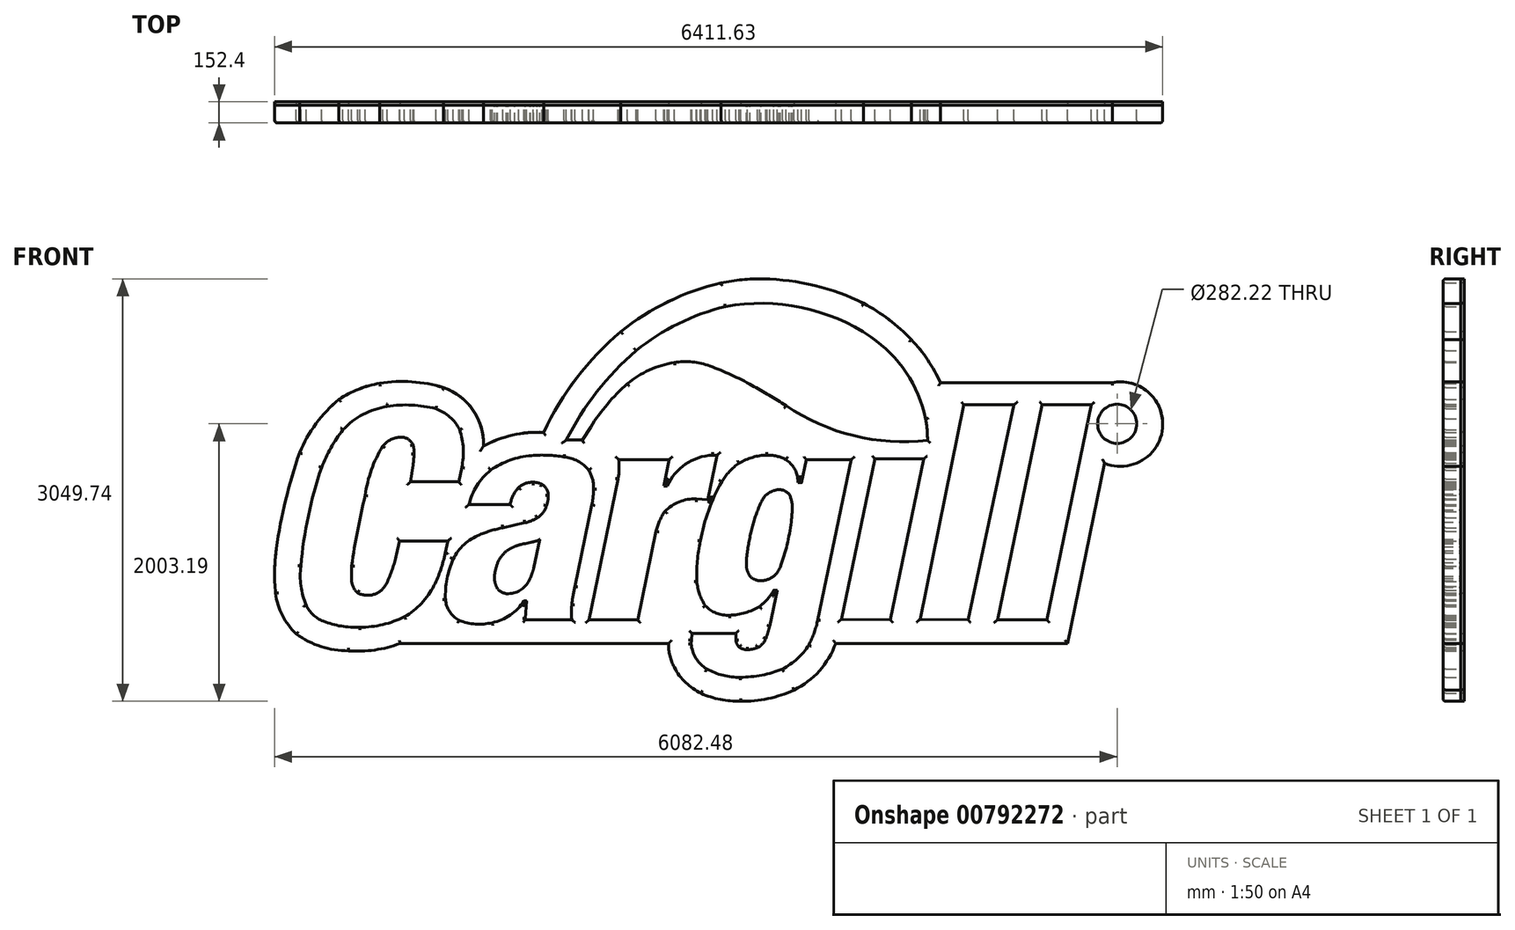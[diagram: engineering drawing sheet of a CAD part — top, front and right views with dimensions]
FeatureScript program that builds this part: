
annotation { "Feature Type Name" : "Feature", "Feature Type Description" : "" }
export const myFeature = defineFeature(function(context is Context, id is Id, definition is map)
    precondition{}
    {
        {
            var Q0;
            Q0=qCreatedBy(makeId("Front.planeOp"),FACE);
            var sketch = newSketch(context, id + "F0", { "sketchPlane" : qUnion([Q0])});
            skArc(sketch, "E0", {"start": v(-1853.74, 164.8) * mm, "mid": v(-1842.63, 301.62) * mm, "end": v(-1868.91, 436.37) * mm});
            skArc(sketch, "E1", {"start": v(-1868.91, 436.37) * mm, "mid": v(-1939.86, 529.44) * mm, "end": v(-2041.08, 588.2) * mm});
            skArc(sketch, "E2", {"start": v(-2041.08, 588.2) * mm, "mid": v(-2215, 614.67) * mm, "end": v(-2390.62, 604.46) * mm});
            skArc(sketch, "E3", {"start": v(-2390.62, 604.46) * mm, "mid": v(-2565.27, 547.67) * mm, "end": v(-2711.35, 436.37) * mm});
            skArc(sketch, "E4", {"start": v(-2711.35, 436.37) * mm, "mid": v(-2798.03, 305.5) * mm, "end": v(-2864.96, 163.5) * mm});
            skArc(sketch, "E5", {"start": v(-2864.96, 163.5) * mm, "mid": v(-2961.53, -187) * mm, "end": v(-3015.73, -546.5) * mm});
            skArc(sketch, "E6", {"start": v(-3015.73, -546.5) * mm, "mid": v(-3014.28, -691.03) * mm, "end": v(-2977.3, -830.75) * mm});
            skArc(sketch, "E7", {"start": v(-2977.3, -830.75) * mm, "mid": v(-2926.34, -899.69) * mm, "end": v(-2853.8, -945.37) * mm});
            skArc(sketch, "E8", {"start": v(-2853.8, -945.37) * mm, "mid": v(-2723.54, -981.4) * mm, "end": v(-2588.63, -989.4) * mm});
            skArc(sketch, "E9", {"start": v(-2588.63, -989.4) * mm, "mid": v(-2423.63, -970.22) * mm, "end": v(-2267.44, -913.67) * mm});
            skArc(sketch, "E10", {"start": v(-2267.44, -913.67) * mm, "mid": v(-2144.2, -816.58) * mm, "end": v(-2054.04, -688.19) * mm});
            skArc(sketch, "E11", {"start": v(-2054.04, -688.19) * mm, "mid": v(-2005.72, -573.66) * mm, "end": v(-1972.93, -453.75) * mm});
            skArc(sketch, "E12", {"start": v(-2395.81, -671.3) * mm, "mid": v(-2354.54, -570.88) * mm, "end": v(-2324.8, -466.47) * mm});
            skArc(sketch, "E13", {"start": v(-2490, -752.83) * mm, "mid": v(-2434.28, -722.02) * mm, "end": v(-2395.81, -671.3) * mm});
            skArc(sketch, "E14", {"start": v(-2605.17, -740.5) * mm, "mid": v(-2548.82, -758.18) * mm, "end": v(-2490, -752.83) * mm});
            skArc(sketch, "E15", {"start": v(-2648.28, -656.13) * mm, "mid": v(-2634.95, -702.52) * mm, "end": v(-2605.17, -740.5) * mm});
            skArc(sketch, "E16", {"start": v(-2648.28, -546.5) * mm, "mid": v(-2650.48, -601.32) * mm, "end": v(-2648.28, -656.13) * mm});
            skArc(sketch, "E17", {"start": v(-2424.98, 317.68) * mm, "mid": v(-2505.79, 147.06) * mm, "end": v(-2550.67, -36.31) * mm});
            skArc(sketch, "E18", {"start": v(-2291.59, 383.09) * mm, "mid": v(-2365.8, 365.72) * mm, "end": v(-2424.98, 317.68) * mm});
            skArc(sketch, "E19", {"start": v(-2205.97, 328.47) * mm, "mid": v(-2240.72, 368.4) * mm, "end": v(-2291.59, 383.09) * mm});
            skArc(sketch, "E20", {"start": v(-2198.16, 261.18) * mm, "mid": v(-2199.1, 295.17) * mm, "end": v(-2205.97, 328.47) * mm});
            skArc(sketch, "E21", {"start": v(-2205.6, 181.3) * mm, "mid": v(-2200.92, 221.14) * mm, "end": v(-2198.16, 261.18) * mm});
            skLineSegment(sketch, "E22", {"start": v(-2205.6, 181.3) * mm, "end": v(-2222.74, 60.72) * mm});
            skLineSegment(sketch, "E23", {"start": v(-2222.74, 60.72) * mm, "end": v(-1875.09, 60.72) * mm});
            skLineSegment(sketch, "E24", {"start": v(-1875.09, 60.72) * mm, "end": v(-1853.74, 164.8) * mm});
            skLineSegment(sketch, "E25", {"start": v(-2324.8, -466.47) * mm, "end": v(-2302.4, -366.84) * mm});
            skLineSegment(sketch, "E26", {"start": v(-2302.4, -366.84) * mm, "end": v(-1954.97, -366.84) * mm});
            skLineSegment(sketch, "E27", {"start": v(-1954.97, -366.84) * mm, "end": v(-1972.93, -453.75) * mm});
            skArc(sketch, "E28", {"start": v(-2550.67, -36.31) * mm, "mid": v(-2606.06, -290.15) * mm, "end": v(-2648.28, -546.5) * mm});
            skLineSegment(sketch, "E29", {"start": v(888.51, -931.26) * mm, "end": v(1128.72, 225.76) * mm});
            skLineSegment(sketch, "E30", {"start": v(1128.72, 225.76) * mm, "end": v(1480.56, 225.76) * mm});
            skLineSegment(sketch, "E31", {"start": v(1480.56, 225.76) * mm, "end": v(1240.36, -934.65) * mm});
            skLineSegment(sketch, "E32", {"start": v(1240.36, -934.65) * mm, "end": v(888.51, -931.26) * mm});
            skLineSegment(sketch, "E33", {"start": v(1454.71, -932.42) * mm, "end": v(1770.63, 615.9) * mm});
            skLineSegment(sketch, "E34", {"start": v(1770.63, 615.9) * mm, "end": v(2132.1, 615.9) * mm});
            skLineSegment(sketch, "E35", {"start": v(2132.1, 615.9) * mm, "end": v(1801.94, -935.26) * mm});
            skLineSegment(sketch, "E36", {"start": v(1801.94, -935.26) * mm, "end": v(1454.71, -932.42) * mm});
            skLineSegment(sketch, "E37", {"start": v(2337.02, 615.9) * mm, "end": v(2015.4, -935.26) * mm});
            skLineSegment(sketch, "E38", {"start": v(2015.4, -935.26) * mm, "end": v(2371.17, -935.26) * mm});
            skLineSegment(sketch, "E39", {"start": v(2371.17, -935.26) * mm, "end": v(2689.94, 615.9) * mm});
            skLineSegment(sketch, "E40", {"start": v(2689.94, 615.9) * mm, "end": v(2337.02, 615.9) * mm});
            skCircle(sketch, "E41", {"center": v(2877.8, 479.28) * mm, "radius": 141.1 * mm});
            skArc(sketch, "E42", {"start": v(-595.08, 1006.86) * mm, "mid": v(-879.13, 709.64) * mm, "end": v(-1098.05, 361.64) * mm});
            skArc(sketch, "E43", {"start": v(50.14, 1325.24) * mm, "mid": v(-290.23, 1202.04) * mm, "end": v(-595.08, 1006.86) * mm});
            skArc(sketch, "E44", {"start": v(1101.08, 1105.47) * mm, "mid": v(597.44, 1319.77) * mm, "end": v(50.14, 1325.24) * mm});
            skArc(sketch, "E45", {"start": v(1495.54, 516.6) * mm, "mid": v(1354.34, 848.57) * mm, "end": v(1101.08, 1105.47) * mm});
            skArc(sketch, "E46", {"start": v(1509.17, 358.66) * mm, "mid": v(1505.54, 437.9) * mm, "end": v(1495.54, 516.6) * mm});
            skArc(sketch, "E47", {"start": v(487.58, 610.95) * mm, "mid": v(975.81, 393.45) * mm, "end": v(1509.17, 358.66) * mm});
            skArc(sketch, "E48", {"start": v(-659.18, 768.54) * mm, "mid": v(-802.03, 621.55) * mm, "end": v(-923.49, 456.45) * mm});
            skArc(sketch, "E49", {"start": v(-318.77, 922.46) * mm, "mid": v(-499.03, 867.74) * mm, "end": v(-659.18, 768.54) * mm});
            skArc(sketch, "E50", {"start": v(-62.13, 896.46) * mm, "mid": v(-188.8, 925.73) * mm, "end": v(-318.77, 922.46) * mm});
            skArc(sketch, "E51", {"start": v(241.27, 757.08) * mm, "mid": v(92.44, 833.01) * mm, "end": v(-62.13, 896.46) * mm});
            skArc(sketch, "E52", {"start": v(487.58, 610.95) * mm, "mid": v(365.23, 685.38) * mm, "end": v(241.27, 757.08) * mm});
            skLineSegment(sketch, "E53", {"start": v(-923.49, 456.45) * mm, "end": v(-983.7, 361.64) * mm});
            skLineSegment(sketch, "E54", {"start": v(-983.7, 361.64) * mm, "end": v(-1098.05, 361.64) * mm});
            skArc(sketch, "E55", {"start": v(2787.2, 194.54) * mm, "mid": v(3205.58, 448.6) * mm, "end": v(2842.16, 776.5) * mm});
            skArc(sketch, "E56", {"start": v(-1645.22, 144.75) * mm, "mid": v(-1743.53, 33.23) * mm, "end": v(-1801.4, -103.72) * mm});
            skArc(sketch, "E57", {"start": v(-1351, 250.45) * mm, "mid": v(-1505.1, 217.08) * mm, "end": v(-1645.22, 144.75) * mm});
            skArc(sketch, "E58", {"start": v(-1114.36, 239.4) * mm, "mid": v(-1232.33, 252.59) * mm, "end": v(-1351, 250.45) * mm});
            skArc(sketch, "E59", {"start": v(-936.89, 144.75) * mm, "mid": v(-1016.16, 209.83) * mm, "end": v(-1114.36, 239.4) * mm});
            skArc(sketch, "E60", {"start": v(-901.92, 8.7) * mm, "mid": v(-909.62, 79.24) * mm, "end": v(-936.89, 144.75) * mm});
            skArc(sketch, "E61", {"start": v(-914.54, -105.31) * mm, "mid": v(-905.3, -48.63) * mm, "end": v(-901.92, 8.7) * mm});
            skArc(sketch, "E62", {"start": v(-1035.83, -693.63) * mm, "mid": v(-1049.72, -759.54) * mm, "end": v(-1058.93, -826.26) * mm});
            skArc(sketch, "E63", {"start": v(-1058.93, -826.26) * mm, "mid": v(-1062.94, -880.8) * mm, "end": v(-1058.93, -935.35) * mm});
            skArc(sketch, "E64", {"start": v(-1634.35, -956.35) * mm, "mid": v(-1503.9, -901.1) * mm, "end": v(-1404.74, -799.92) * mm});
            skArc(sketch, "E65", {"start": v(-1873.12, -938.04) * mm, "mid": v(-1755.2, -966.35) * mm, "end": v(-1634.35, -956.35) * mm});
            skArc(sketch, "E66", {"start": v(-1971.27, -789.36) * mm, "mid": v(-1941.6, -876.52) * mm, "end": v(-1873.12, -938.04) * mm});
            skArc(sketch, "E67", {"start": v(-1915, -497.35) * mm, "mid": v(-1960.34, -640.04) * mm, "end": v(-1971.27, -789.36) * mm});
            skArc(sketch, "E68", {"start": v(-1724.64, -321.62) * mm, "mid": v(-1835.8, -392.18) * mm, "end": v(-1915, -497.35) * mm});
            skArc(sketch, "E69", {"start": v(-1556.88, -270.9) * mm, "mid": v(-1642.04, -292.02) * mm, "end": v(-1724.64, -321.62) * mm});
            skArc(sketch, "E70", {"start": v(-1242.46, -113.42) * mm, "mid": v(-1232.17, -75.81) * mm, "end": v(-1229.71, -36.9) * mm});
            skArc(sketch, "E71", {"start": v(-1229.71, -36.9) * mm, "mid": v(-1241.56, 9.56) * mm, "end": v(-1275.57, 43.36) * mm});
            skArc(sketch, "E72", {"start": v(-1275.57, 43.36) * mm, "mid": v(-1305.97, 54.07) * mm, "end": v(-1338.06, 57.12) * mm});
            skArc(sketch, "E73", {"start": v(-1338.06, 57.12) * mm, "mid": v(-1394.55, 48.2) * mm, "end": v(-1443.54, 18.7) * mm});
            skArc(sketch, "E74", {"start": v(-1443.54, 18.7) * mm, "mid": v(-1482.62, -37.61) * mm, "end": v(-1503.74, -102.83) * mm});
            skLineSegment(sketch, "E75", {"start": v(-1801.4, -103.72) * mm, "end": v(-1503.74, -102.83) * mm});
            skArc(sketch, "E76", {"start": v(-1308.09, -199.85) * mm, "mid": v(-1267.42, -162.6) * mm, "end": v(-1242.46, -113.42) * mm});
            skArc(sketch, "E77", {"start": v(-1398.04, -235.27) * mm, "mid": v(-1351.72, -220.98) * mm, "end": v(-1308.09, -199.85) * mm});
            skLineSegment(sketch, "E78", {"start": v(-1556.88, -270.9) * mm, "end": v(-1398.04, -235.27) * mm});
            skLineSegment(sketch, "E79", {"start": v(-1035.83, -693.63) * mm, "end": v(-914.54, -105.31) * mm});
            skLineSegment(sketch, "E80", {"start": v(-1058.93, -935.35) * mm, "end": v(-1393.05, -935.35) * mm});
            skLineSegment(sketch, "E81", {"start": v(-1393.05, -935.35) * mm, "end": v(-1393.66, -925.25) * mm});
            skLineSegment(sketch, "E82", {"start": v(-1393.66, -925.25) * mm, "end": v(-1385.77, -799.35) * mm});
            skLineSegment(sketch, "E83", {"start": v(-1385.77, -799.35) * mm, "end": v(-1404.74, -799.92) * mm});
            skArc(sketch, "E84", {"start": v(-1517.46, -747.03) * mm, "mid": v(-1422.59, -716.33) * mm, "end": v(-1360.21, -638.53) * mm});
            skArc(sketch, "E85", {"start": v(-1360.21, -638.53) * mm, "mid": v(-1345.94, -601.96) * mm, "end": v(-1334.75, -564.32) * mm});
            skArc(sketch, "E86", {"start": v(-1600.82, -701.27) * mm, "mid": v(-1565.62, -735.95) * mm, "end": v(-1517.46, -747.03) * mm});
            skArc(sketch, "E87", {"start": v(-1617.05, -621.91) * mm, "mid": v(-1614.45, -662.72) * mm, "end": v(-1600.82, -701.27) * mm});
            skArc(sketch, "E88", {"start": v(-1593.8, -522.98) * mm, "mid": v(-1608.96, -571.62) * mm, "end": v(-1617.05, -621.91) * mm});
            skArc(sketch, "E89", {"start": v(-1529.83, -438.31) * mm, "mid": v(-1566.7, -476.96) * mm, "end": v(-1593.8, -522.98) * mm});
            skArc(sketch, "E90", {"start": v(-1472.28, -406.96) * mm, "mid": v(-1501.86, -421.16) * mm, "end": v(-1529.83, -438.31) * mm});
            skArc(sketch, "E91", {"start": v(-1395.4, -384.73) * mm, "mid": v(-1434.41, -393.86) * mm, "end": v(-1472.28, -406.96) * mm});
            skArc(sketch, "E92", {"start": v(-1356.2, -376.5) * mm, "mid": v(-1333.26, -371.34) * mm, "end": v(-1310.69, -364.8) * mm});
            skArc(sketch, "E93", {"start": v(-1310.69, -364.8) * mm, "mid": v(-1300.48, -359.9) * mm, "end": v(-1291.06, -353.65) * mm});
            skLineSegment(sketch, "E94", {"start": v(-1291.06, -353.65) * mm, "end": v(-1289.84, -353.65) * mm});
            skLineSegment(sketch, "E95", {"start": v(-1289.84, -353.65) * mm, "end": v(-1334.75, -564.32) * mm});
            skLineSegment(sketch, "E96", {"start": v(-1395.4, -384.73) * mm, "end": v(-1356.2, -376.5) * mm});
            skArc(sketch, "E97", {"start": v(-387.94, -153.2) * mm, "mid": v(-425.7, -221.92) * mm, "end": v(-450.55, -296.3) * mm});
            skArc(sketch, "E98", {"start": v(-160.28, -62.94) * mm, "mid": v(-283.64, -84.04) * mm, "end": v(-387.94, -153.2) * mm});
            skArc(sketch, "E99", {"start": v(-42.88, 253.05) * mm, "mid": v(-237.67, 187.9) * mm, "end": v(-370.17, 30.95) * mm});
            skArc(sketch, "E100", {"start": v(-724.98, 80.6) * mm, "mid": v(-717.66, 151.06) * mm, "end": v(-720.65, 221.83) * mm});
            skLineSegment(sketch, "E101", {"start": v(-720.65, 221.83) * mm, "end": v(-356.51, 221.83) * mm});
            skLineSegment(sketch, "E102", {"start": v(-356.51, 221.83) * mm, "end": v(-395.89, 30.95) * mm});
            skLineSegment(sketch, "E103", {"start": v(-395.89, 30.95) * mm, "end": v(-370.17, 30.95) * mm});
            skLineSegment(sketch, "E104", {"start": v(-160.28, -62.94) * mm, "end": v(-77.7, -69.74) * mm});
            skLineSegment(sketch, "E105", {"start": v(-77.7, -69.74) * mm, "end": v(-10.97, 253.27) * mm});
            skLineSegment(sketch, "E106", {"start": v(-10.97, 253.27) * mm, "end": v(-42.88, 253.05) * mm});
            skLineSegment(sketch, "E107", {"start": v(-724.98, 80.6) * mm, "end": v(-933.72, -935.84) * mm});
            skLineSegment(sketch, "E108", {"start": v(-933.72, -935.84) * mm, "end": v(-582.85, -935.84) * mm});
            skLineSegment(sketch, "E109", {"start": v(-582.85, -935.84) * mm, "end": v(-450.55, -296.3) * mm});
            skArc(sketch, "E110", {"start": v(-197.36, -1108.56) * mm, "mid": v(-162.64, -1213.34) * mm, "end": v(-84.09, -1290.87) * mm});
            skArc(sketch, "E111", {"start": v(-84.09, -1290.87) * mm, "mid": v(32.73, -1336.3) * mm, "end": v(157.28, -1350.3) * mm});
            skArc(sketch, "E112", {"start": v(157.28, -1350.3) * mm, "mid": v(312.42, -1335.05) * mm, "end": v(461.93, -1290.87) * mm});
            skArc(sketch, "E113", {"start": v(461.93, -1290.87) * mm, "mid": v(568.6, -1216.6) * mm, "end": v(652.22, -1117.08) * mm});
            skArc(sketch, "E114", {"start": v(652.22, -1117.08) * mm, "mid": v(690.73, -1028.55) * mm, "end": v(716.96, -935.64) * mm});
            skArc(sketch, "E115", {"start": v(572.85, 76.64) * mm, "mid": v(546.3, 158.5) * mm, "end": v(486.42, 220.31) * mm});
            skArc(sketch, "E116", {"start": v(486.42, 220.31) * mm, "mid": v(420.25, 246) * mm, "end": v(349.65, 253.33) * mm});
            skArc(sketch, "E117", {"start": v(349.65, 253.33) * mm, "mid": v(245.43, 237.66) * mm, "end": v(148.88, 195.38) * mm});
            skArc(sketch, "E118", {"start": v(148.88, 195.38) * mm, "mid": v(78.8, 134.98) * mm, "end": v(23.09, 61.1) * mm});
            skArc(sketch, "E119", {"start": v(23.09, 61.1) * mm, "mid": v(-71.74, -146.6) * mm, "end": v(-131.48, -366.99) * mm});
            skArc(sketch, "E120", {"start": v(-131.48, -366.99) * mm, "mid": v(-152.88, -512.22) * mm, "end": v(-156.62, -658.97) * mm});
            skArc(sketch, "E121", {"start": v(-156.62, -658.97) * mm, "mid": v(-137.02, -749.7) * mm, "end": v(-95.54, -832.74) * mm});
            skArc(sketch, "E122", {"start": v(-95.54, -832.74) * mm, "mid": v(-16.22, -887.84) * mm, "end": v(79.28, -902.25) * mm});
            skArc(sketch, "E123", {"start": v(79.28, -902.25) * mm, "mid": v(192.1, -884.73) * mm, "end": v(297, -839.73) * mm});
            skArc(sketch, "E124", {"start": v(297, -839.73) * mm, "mid": v(349.1, -791.48) * mm, "end": v(391.28, -734.35) * mm});
            skArc(sketch, "E125", {"start": v(125.8, -1081.2) * mm, "mid": v(132.95, -1110.4) * mm, "end": v(151.27, -1134.24) * mm});
            skArc(sketch, "E126", {"start": v(151.27, -1134.24) * mm, "mid": v(178.83, -1147.69) * mm, "end": v(209.3, -1151.25) * mm});
            skArc(sketch, "E127", {"start": v(209.3, -1151.25) * mm, "mid": v(245.77, -1147.43) * mm, "end": v(280.95, -1137.05) * mm});
            skArc(sketch, "E128", {"start": v(280.95, -1137.05) * mm, "mid": v(317.27, -1109.33) * mm, "end": v(341.79, -1070.79) * mm});
            skArc(sketch, "E129", {"start": v(341.79, -1070.79) * mm, "mid": v(357.27, -1026.34) * mm, "end": v(369.87, -980.98) * mm});
            skArc(sketch, "E130", {"start": v(228.15, -621.33) * mm, "mid": v(263.51, -645.84) * mm, "end": v(305.86, -653.44) * mm});
            skArc(sketch, "E131", {"start": v(305.86, -653.44) * mm, "mid": v(354.88, -644.95) * mm, "end": v(398.92, -621.8) * mm});
            skArc(sketch, "E132", {"start": v(398.92, -621.8) * mm, "mid": v(426.46, -590.15) * mm, "end": v(446.1, -553.08) * mm});
            skArc(sketch, "E133", {"start": v(446.1, -553.08) * mm, "mid": v(495, -394.18) * mm, "end": v(524.3, -230.53) * mm});
            skArc(sketch, "E134", {"start": v(202.74, -560.17) * mm, "mid": v(211.76, -592.28) * mm, "end": v(228.15, -621.33) * mm});
            skArc(sketch, "E135", {"start": v(207.4, -451.93) * mm, "mid": v(202.15, -505.92) * mm, "end": v(202.74, -560.17) * mm});
            skArc(sketch, "E136", {"start": v(246.22, -257.29) * mm, "mid": v(224, -354.05) * mm, "end": v(207.4, -451.93) * mm});
            skArc(sketch, "E137", {"start": v(311.71, -78.12) * mm, "mid": v(274.52, -166.08) * mm, "end": v(246.22, -257.29) * mm});
            skArc(sketch, "E138", {"start": v(434.98, 3.76) * mm, "mid": v(362.16, -20.34) * mm, "end": v(311.71, -78.12) * mm});
            skArc(sketch, "E139", {"start": v(508.94, -27.5) * mm, "mid": v(475.45, -3.61) * mm, "end": v(434.98, 3.76) * mm});
            skArc(sketch, "E140", {"start": v(532.27, -140.63) * mm, "mid": v(528.63, -82.4) * mm, "end": v(508.94, -27.5) * mm});
            skArc(sketch, "E141", {"start": v(524.3, -230.53) * mm, "mid": v(529.17, -185.66) * mm, "end": v(532.27, -140.63) * mm});
            skLineSegment(sketch, "E142", {"start": v(572.85, 76.64) * mm, "end": v(574.8, 53.82) * mm});
            skLineSegment(sketch, "E143", {"start": v(574.8, 53.82) * mm, "end": v(599.34, 53.82) * mm});
            skLineSegment(sketch, "E144", {"start": v(599.34, 53.82) * mm, "end": v(633.67, 221.52) * mm});
            skLineSegment(sketch, "E145", {"start": v(633.67, 221.52) * mm, "end": v(957.92, 221.52) * mm});
            skLineSegment(sketch, "E146", {"start": v(957.92, 221.52) * mm, "end": v(716.96, -935.64) * mm});
            skLineSegment(sketch, "E147", {"start": v(391.28, -734.35) * mm, "end": v(398.54, -722.3) * mm});
            skLineSegment(sketch, "E148", {"start": v(398.54, -722.3) * mm, "end": v(423.93, -722.3) * mm});
            skLineSegment(sketch, "E149", {"start": v(423.93, -722.3) * mm, "end": v(369.87, -980.98) * mm});
            skLineSegment(sketch, "E150", {"start": v(-197.36, -1108.56) * mm, "end": v(-196.23, -1081.82) * mm});
            skLineSegment(sketch, "E151", {"start": v(-196.23, -1081.82) * mm, "end": v(-192.26, -1034.4) * mm});
            skLineSegment(sketch, "E152", {"start": v(-192.26, -1034.4) * mm, "end": v(124.38, -1034.4) * mm});
            skLineSegment(sketch, "E153", {"start": v(124.38, -1034.4) * mm, "end": v(125.8, -1081.2) * mm});
            skArc(sketch, "E154", {"start": v(-1263.1, 417.63) * mm, "mid": v(-1486.7, 397.65) * mm, "end": v(-1696.84, 318.74) * mm});
            skArc(sketch, "E155", {"start": v(-705.45, 1144.69) * mm, "mid": v(-1022.9, 810.79) * mm, "end": v(-1263.1, 417.63) * mm});
            skArc(sketch, "E156", {"start": v(19.35, 1496.35) * mm, "mid": v(-362.9, 1361.42) * mm, "end": v(-705.45, 1144.69) * mm});
            skArc(sketch, "E157", {"start": v(323.6, 1525.23) * mm, "mid": v(170.65, 1519.57) * mm, "end": v(19.35, 1496.35) * mm});
            skArc(sketch, "E158", {"start": v(1047.44, 1348.95) * mm, "mid": v(695.27, 1477.13) * mm, "end": v(323.6, 1525.23) * mm});
            skArc(sketch, "E159", {"start": v(1393.05, 1086.56) * mm, "mid": v(1230.52, 1231.28) * mm, "end": v(1047.44, 1348.95) * mm});
            skArc(sketch, "E160", {"start": v(1602.17, 775) * mm, "mid": v(1510.4, 939.36) * mm, "end": v(1393.05, 1086.56) * mm});
            skArc(sketch, "E161", {"start": v(545.8, -1442) * mm, "mid": v(729, -1303.68) * mm, "end": v(845.4, -1105.82) * mm});
            skArc(sketch, "E162", {"start": v(159.26, -1523.77) * mm, "mid": v(357.17, -1504.82) * mm, "end": v(545.8, -1442) * mm});
            skArc(sketch, "E163", {"start": v(-125.64, -1466.52) * mm, "mid": v(13.7, -1510.67) * mm, "end": v(159.26, -1523.77) * mm});
            skArc(sketch, "E164", {"start": v(-318.78, -1279.88) * mm, "mid": v(-237.12, -1388.63) * mm, "end": v(-125.64, -1466.52) * mm});
            skArc(sketch, "E165", {"start": v(-361.08, -1106.17) * mm, "mid": v(-350.53, -1195.6) * mm, "end": v(-318.78, -1279.88) * mm});
            skArc(sketch, "E166", {"start": v(-2671.49, -1159.6) * mm, "mid": v(-2482.3, -1153.33) * mm, "end": v(-2298.96, -1106.17) * mm});
            skArc(sketch, "E167", {"start": v(-3048.27, -1038.38) * mm, "mid": v(-2869.55, -1129.07) * mm, "end": v(-2671.49, -1159.6) * mm});
            skArc(sketch, "E168", {"start": v(-3197.9, -743.94) * mm, "mid": v(-3148.07, -903.86) * mm, "end": v(-3048.27, -1038.38) * mm});
            skArc(sketch, "E169", {"start": v(-3191.63, -420.1) * mm, "mid": v(-3204.43, -581.83) * mm, "end": v(-3197.9, -743.94) * mm});
            skArc(sketch, "E170", {"start": v(-3024.7, 270.66) * mm, "mid": v(-3124.62, -70.74) * mm, "end": v(-3191.63, -420.1) * mm});
            skArc(sketch, "E171", {"start": v(-2739.83, 655.5) * mm, "mid": v(-2905.7, 480.43) * mm, "end": v(-3024.7, 270.66) * mm});
            skArc(sketch, "E172", {"start": v(-2446.08, 771.91) * mm, "mid": v(-2598.96, 728.86) * mm, "end": v(-2739.83, 655.5) * mm});
            skArc(sketch, "E173", {"start": v(-1984.48, 740.78) * mm, "mid": v(-2213.5, 782.59) * mm, "end": v(-2446.08, 771.91) * mm});
            skArc(sketch, "E174", {"start": v(-1696.84, 318.74) * mm, "mid": v(-1771.44, 576.93) * mm, "end": v(-1984.48, 740.78) * mm});
            skLineSegment(sketch, "E175", {"start": v(845.4, -1105.82) * mm, "end": v(2520.06, -1105.82) * mm});
            skLineSegment(sketch, "E176", {"start": v(2520.06, -1105.82) * mm, "end": v(2787.2, 194.54) * mm});
            skLineSegment(sketch, "E177", {"start": v(2842.16, 776.5) * mm, "end": v(1602.17, 775) * mm});
            skLineSegment(sketch, "E178", {"start": v(-361.08, -1106.17) * mm, "end": v(-2298.96, -1106.17) * mm});
            skSolve(sketch);
        }
        {
            var Q0;
            Q0=qCreatedBy(makeId("Front.planeOp"),FACE);
            var sketch = newSketch(context, id + "F1", { "sketchPlane" : qUnion([Q0])});
            skArc(sketch, "E179", {"start": v(-1263.1, 417.94) * mm, "mid": v(-1486.68, 397.96) * mm, "end": v(-1696.83, 319.05) * mm});
            skArc(sketch, "E180", {"start": v(-705.45, 1145) * mm, "mid": v(-1022.9, 811.1) * mm, "end": v(-1263.1, 417.94) * mm});
            skArc(sketch, "E181", {"start": v(19.36, 1496.66) * mm, "mid": v(-362.89, 1361.73) * mm, "end": v(-705.45, 1145) * mm});
            skArc(sketch, "E182", {"start": v(323.61, 1525.55) * mm, "mid": v(170.65, 1519.88) * mm, "end": v(19.36, 1496.66) * mm});
            skArc(sketch, "E183", {"start": v(1047.44, 1349.26) * mm, "mid": v(695.28, 1477.45) * mm, "end": v(323.61, 1525.55) * mm});
            skArc(sketch, "E184", {"start": v(1393.06, 1086.88) * mm, "mid": v(1230.52, 1231.6) * mm, "end": v(1047.44, 1349.26) * mm});
            skArc(sketch, "E185", {"start": v(1602.18, 775.3) * mm, "mid": v(1510.4, 939.67) * mm, "end": v(1393.06, 1086.88) * mm});
            skArc(sketch, "E186", {"start": v(2787.22, 194.85) * mm, "mid": v(3205.6, 448.92) * mm, "end": v(2842.17, 776.81) * mm});
            skArc(sketch, "E187", {"start": v(545.81, -1441.69) * mm, "mid": v(729.01, -1303.36) * mm, "end": v(845.41, -1105.5) * mm});
            skArc(sketch, "E188", {"start": v(159.26, -1523.46) * mm, "mid": v(357.18, -1504.5) * mm, "end": v(545.81, -1441.69) * mm});
            skArc(sketch, "E189", {"start": v(-125.63, -1466.2) * mm, "mid": v(13.7, -1510.36) * mm, "end": v(159.26, -1523.46) * mm});
            skArc(sketch, "E190", {"start": v(-318.77, -1279.57) * mm, "mid": v(-237.11, -1388.32) * mm, "end": v(-125.63, -1466.2) * mm});
            skArc(sketch, "E191", {"start": v(-361.07, -1105.85) * mm, "mid": v(-350.52, -1195.3) * mm, "end": v(-318.77, -1279.57) * mm});
            skArc(sketch, "E192", {"start": v(-2671.48, -1159.3) * mm, "mid": v(-2482.29, -1153.02) * mm, "end": v(-2298.96, -1105.85) * mm});
            skArc(sketch, "E193", {"start": v(-3048.26, -1038.07) * mm, "mid": v(-2869.55, -1128.76) * mm, "end": v(-2671.48, -1159.3) * mm});
            skArc(sketch, "E194", {"start": v(-3197.9, -743.62) * mm, "mid": v(-3148.06, -903.54) * mm, "end": v(-3048.26, -1038.07) * mm});
            skArc(sketch, "E195", {"start": v(-3191.62, -419.78) * mm, "mid": v(-3204.43, -581.52) * mm, "end": v(-3197.9, -743.62) * mm});
            skArc(sketch, "E196", {"start": v(-3024.7, 270.97) * mm, "mid": v(-3124.61, -70.43) * mm, "end": v(-3191.62, -419.78) * mm});
            skArc(sketch, "E197", {"start": v(-2739.82, 655.81) * mm, "mid": v(-2905.7, 480.74) * mm, "end": v(-3024.7, 270.97) * mm});
            skArc(sketch, "E198", {"start": v(-2446.07, 772.23) * mm, "mid": v(-2598.95, 729.17) * mm, "end": v(-2739.82, 655.81) * mm});
            skArc(sketch, "E199", {"start": v(-1984.47, 741.1) * mm, "mid": v(-2213.5, 782.9) * mm, "end": v(-2446.07, 772.23) * mm});
            skArc(sketch, "E200", {"start": v(-1696.83, 319.05) * mm, "mid": v(-1771.43, 577.25) * mm, "end": v(-1984.47, 741.1) * mm});
            skLineSegment(sketch, "E201", {"start": v(845.41, -1105.5) * mm, "end": v(2520.06, -1105.5) * mm});
            skLineSegment(sketch, "E202", {"start": v(2520.06, -1105.5) * mm, "end": v(2787.22, 194.85) * mm});
            skLineSegment(sketch, "E203", {"start": v(2842.17, 776.81) * mm, "end": v(1602.18, 775.3) * mm});
            skLineSegment(sketch, "E204", {"start": v(-361.07, -1105.85) * mm, "end": v(-2298.96, -1105.85) * mm});
            skSolve(sketch);
        }
        {
            var Q0;
            Q0=makeQuery(id+"F0.imprint","IMPRINT",FACE,{"disambiguationData":[TD([[makeQuery(id+"F0.imprint","IMPRINT",EDGE,{"derivedFrom":sQuery(id+"F0.wireOp",EDGE,"E0")}),-1.0]])]});
            var Q1;
            Q1=makeQuery(id+"F0.imprint","IMPRINT",FACE,{"disambiguationData":[TD([[makeQuery(id+"F0.imprint","IMPRINT",EDGE,{"derivedFrom":sQuery(id+"F0.wireOp",EDGE,"E84")}),1.0]])]});
            var Q2;
            Q2=makeQuery(id+"F0.imprint","IMPRINT",FACE,{"disambiguationData":[TD([[makeQuery(id+"F0.imprint","IMPRINT",EDGE,{"derivedFrom":sQuery(id+"F0.wireOp",EDGE,"E130")}),1.0]])]});
            extrude(context, id + "F2", {"entities" : qUnion([Q0, Q1, Q2]), "depth" : 127 * mm, "offsetDistance" : 25.4 * mm});
        }
        {
            var Q0;
            Q0=makeQuery(id+"F2.opExtrude","CAP_FACE",FACE,{"disambiguationData":[OSD([sQuery(id+"F0.wireOp",EDGE,"E0"),sQuery(id+"F0.wireOp",EDGE,"E1"),sQuery(id+"F0.wireOp",EDGE,"E2"),sQuery(id+"F0.wireOp",EDGE,"E3"),sQuery(id+"F0.wireOp",EDGE,"E4"),sQuery(id+"F0.wireOp",EDGE,"E5"),sQuery(id+"F0.wireOp",EDGE,"E6"),sQuery(id+"F0.wireOp",EDGE,"E7"),sQuery(id+"F0.wireOp",EDGE,"E8"),sQuery(id+"F0.wireOp",EDGE,"E9"),sQuery(id+"F0.wireOp",EDGE,"E10"),sQuery(id+"F0.wireOp",EDGE,"E11"),sQuery(id+"F0.wireOp",EDGE,"E12"),sQuery(id+"F0.wireOp",EDGE,"E13"),sQuery(id+"F0.wireOp",EDGE,"E14"),sQuery(id+"F0.wireOp",EDGE,"E15"),sQuery(id+"F0.wireOp",EDGE,"E16"),sQuery(id+"F0.wireOp",EDGE,"E17"),sQuery(id+"F0.wireOp",EDGE,"E18"),sQuery(id+"F0.wireOp",EDGE,"E19"),sQuery(id+"F0.wireOp",EDGE,"E20"),sQuery(id+"F0.wireOp",EDGE,"E21"),sQuery(id+"F0.wireOp",EDGE,"E22"),sQuery(id+"F0.wireOp",EDGE,"E23"),sQuery(id+"F0.wireOp",EDGE,"E24"),sQuery(id+"F0.wireOp",EDGE,"E25"),sQuery(id+"F0.wireOp",EDGE,"E26"),sQuery(id+"F0.wireOp",EDGE,"E27"),sQuery(id+"F0.wireOp",EDGE,"E28"),sQuery(id+"F0.wireOp",EDGE,"E29"),sQuery(id+"F0.wireOp",EDGE,"E30"),sQuery(id+"F0.wireOp",EDGE,"E31"),sQuery(id+"F0.wireOp",EDGE,"E32"),sQuery(id+"F0.wireOp",EDGE,"E33"),sQuery(id+"F0.wireOp",EDGE,"E34"),sQuery(id+"F0.wireOp",EDGE,"E35"),sQuery(id+"F0.wireOp",EDGE,"E36"),sQuery(id+"F0.wireOp",EDGE,"E37"),sQuery(id+"F0.wireOp",EDGE,"E38"),sQuery(id+"F0.wireOp",EDGE,"E39"),sQuery(id+"F0.wireOp",EDGE,"E40"),sQuery(id+"F0.wireOp",EDGE,"E41"),sQuery(id+"F0.wireOp",EDGE,"E42"),sQuery(id+"F0.wireOp",EDGE,"E43"),sQuery(id+"F0.wireOp",EDGE,"E44"),sQuery(id+"F0.wireOp",EDGE,"E45"),sQuery(id+"F0.wireOp",EDGE,"E46"),sQuery(id+"F0.wireOp",EDGE,"E47"),sQuery(id+"F0.wireOp",EDGE,"E48"),sQuery(id+"F0.wireOp",EDGE,"E49"),sQuery(id+"F0.wireOp",EDGE,"E50"),sQuery(id+"F0.wireOp",EDGE,"E51"),sQuery(id+"F0.wireOp",EDGE,"E52"),sQuery(id+"F0.wireOp",EDGE,"E53"),sQuery(id+"F0.wireOp",EDGE,"E54"),sQuery(id+"F0.wireOp",EDGE,"E56"),sQuery(id+"F0.wireOp",EDGE,"E57"),sQuery(id+"F0.wireOp",EDGE,"E58"),sQuery(id+"F0.wireOp",EDGE,"E59"),sQuery(id+"F0.wireOp",EDGE,"E60"),sQuery(id+"F0.wireOp",EDGE,"E61"),sQuery(id+"F0.wireOp",EDGE,"E62"),sQuery(id+"F0.wireOp",EDGE,"E63"),sQuery(id+"F0.wireOp",EDGE,"E64"),sQuery(id+"F0.wireOp",EDGE,"E65"),sQuery(id+"F0.wireOp",EDGE,"E66"),sQuery(id+"F0.wireOp",EDGE,"E67"),sQuery(id+"F0.wireOp",EDGE,"E68"),sQuery(id+"F0.wireOp",EDGE,"E69"),sQuery(id+"F0.wireOp",EDGE,"E70"),sQuery(id+"F0.wireOp",EDGE,"E71"),sQuery(id+"F0.wireOp",EDGE,"E72"),sQuery(id+"F0.wireOp",EDGE,"E73"),sQuery(id+"F0.wireOp",EDGE,"E74"),sQuery(id+"F0.wireOp",EDGE,"E75"),sQuery(id+"F0.wireOp",EDGE,"E76"),sQuery(id+"F0.wireOp",EDGE,"E77"),sQuery(id+"F0.wireOp",EDGE,"E78"),sQuery(id+"F0.wireOp",EDGE,"E79"),sQuery(id+"F0.wireOp",EDGE,"E80"),sQuery(id+"F0.wireOp",EDGE,"E81"),sQuery(id+"F0.wireOp",EDGE,"E82"),sQuery(id+"F0.wireOp",EDGE,"E83"),sQuery(id+"F0.wireOp",EDGE,"E97"),sQuery(id+"F0.wireOp",EDGE,"E98"),sQuery(id+"F0.wireOp",EDGE,"E99"),sQuery(id+"F0.wireOp",EDGE,"E100"),sQuery(id+"F0.wireOp",EDGE,"E101"),sQuery(id+"F0.wireOp",EDGE,"E102"),sQuery(id+"F0.wireOp",EDGE,"E103"),sQuery(id+"F0.wireOp",EDGE,"E104"),sQuery(id+"F0.wireOp",EDGE,"E105"),sQuery(id+"F0.wireOp",EDGE,"E106"),sQuery(id+"F0.wireOp",EDGE,"E107"),sQuery(id+"F0.wireOp",EDGE,"E108"),sQuery(id+"F0.wireOp",EDGE,"E109"),sQuery(id+"F0.wireOp",EDGE,"E110"),sQuery(id+"F0.wireOp",EDGE,"E111"),sQuery(id+"F0.wireOp",EDGE,"E112"),sQuery(id+"F0.wireOp",EDGE,"E113"),sQuery(id+"F0.wireOp",EDGE,"E114"),sQuery(id+"F0.wireOp",EDGE,"E115"),sQuery(id+"F0.wireOp",EDGE,"E116"),sQuery(id+"F0.wireOp",EDGE,"E117"),sQuery(id+"F0.wireOp",EDGE,"E118"),sQuery(id+"F0.wireOp",EDGE,"E119"),sQuery(id+"F0.wireOp",EDGE,"E120"),sQuery(id+"F0.wireOp",EDGE,"E121"),sQuery(id+"F0.wireOp",EDGE,"E122"),sQuery(id+"F0.wireOp",EDGE,"E123"),sQuery(id+"F0.wireOp",EDGE,"E124"),sQuery(id+"F0.wireOp",EDGE,"E125"),sQuery(id+"F0.wireOp",EDGE,"E126"),sQuery(id+"F0.wireOp",EDGE,"E127"),sQuery(id+"F0.wireOp",EDGE,"E128"),sQuery(id+"F0.wireOp",EDGE,"E129"),sQuery(id+"F0.wireOp",EDGE,"E142"),sQuery(id+"F0.wireOp",EDGE,"E143"),sQuery(id+"F0.wireOp",EDGE,"E144"),sQuery(id+"F0.wireOp",EDGE,"E145"),sQuery(id+"F0.wireOp",EDGE,"E146"),sQuery(id+"F0.wireOp",EDGE,"E147"),sQuery(id+"F0.wireOp",EDGE,"E148"),sQuery(id+"F0.wireOp",EDGE,"E149"),sQuery(id+"F0.wireOp",EDGE,"E150"),sQuery(id+"F0.wireOp",EDGE,"E151"),sQuery(id+"F0.wireOp",EDGE,"E152"),sQuery(id+"F0.wireOp",EDGE,"E153"),sQuery(id+"F0.wireOp",EDGE,"E154"),sQuery(id+"F0.wireOp",EDGE,"E155"),sQuery(id+"F0.wireOp",EDGE,"E156"),sQuery(id+"F0.wireOp",EDGE,"E157"),sQuery(id+"F0.wireOp",EDGE,"E158"),sQuery(id+"F0.wireOp",EDGE,"E159"),sQuery(id+"F0.wireOp",EDGE,"E160"),sQuery(id+"F0.wireOp",EDGE,"E55"),sQuery(id+"F0.wireOp",EDGE,"E161"),sQuery(id+"F0.wireOp",EDGE,"E162"),sQuery(id+"F0.wireOp",EDGE,"E163"),sQuery(id+"F0.wireOp",EDGE,"E164"),sQuery(id+"F0.wireOp",EDGE,"E165"),sQuery(id+"F0.wireOp",EDGE,"E166"),sQuery(id+"F0.wireOp",EDGE,"E167"),sQuery(id+"F0.wireOp",EDGE,"E168"),sQuery(id+"F0.wireOp",EDGE,"E169"),sQuery(id+"F0.wireOp",EDGE,"E170"),sQuery(id+"F0.wireOp",EDGE,"E171"),sQuery(id+"F0.wireOp",EDGE,"E172"),sQuery(id+"F0.wireOp",EDGE,"E173"),sQuery(id+"F0.wireOp",EDGE,"E174"),sQuery(id+"F0.wireOp",EDGE,"E175"),sQuery(id+"F0.wireOp",EDGE,"E176"),sQuery(id+"F0.wireOp",EDGE,"E177"),sQuery(id+"F0.wireOp",EDGE,"E178")])],"isStart":false});
            fillet(context, id + "F3", {"entities" : qUnion([Q0]), "radius" : 20.32 * mm, "tangentPropagation" : true, "allowEdgeOverflow" : false});
        }
        {
            var Q0;
            Q0=makeQuery(id+"F1.imprint","IMPRINT",FACE,{"disambiguationData":[TD([[makeQuery(id+"F1.imprint","IMPRINT",EDGE,{"derivedFrom":sQuery(id+"F1.wireOp",EDGE,"E179")}),1.0]])]});
            extrude(context, id + "F4", {"entities" : qUnion([Q0]), "oppositeDirection" : true, "depth" : 25.4 * mm, "offsetDistance" : 25.4 * mm});
        }
    });
